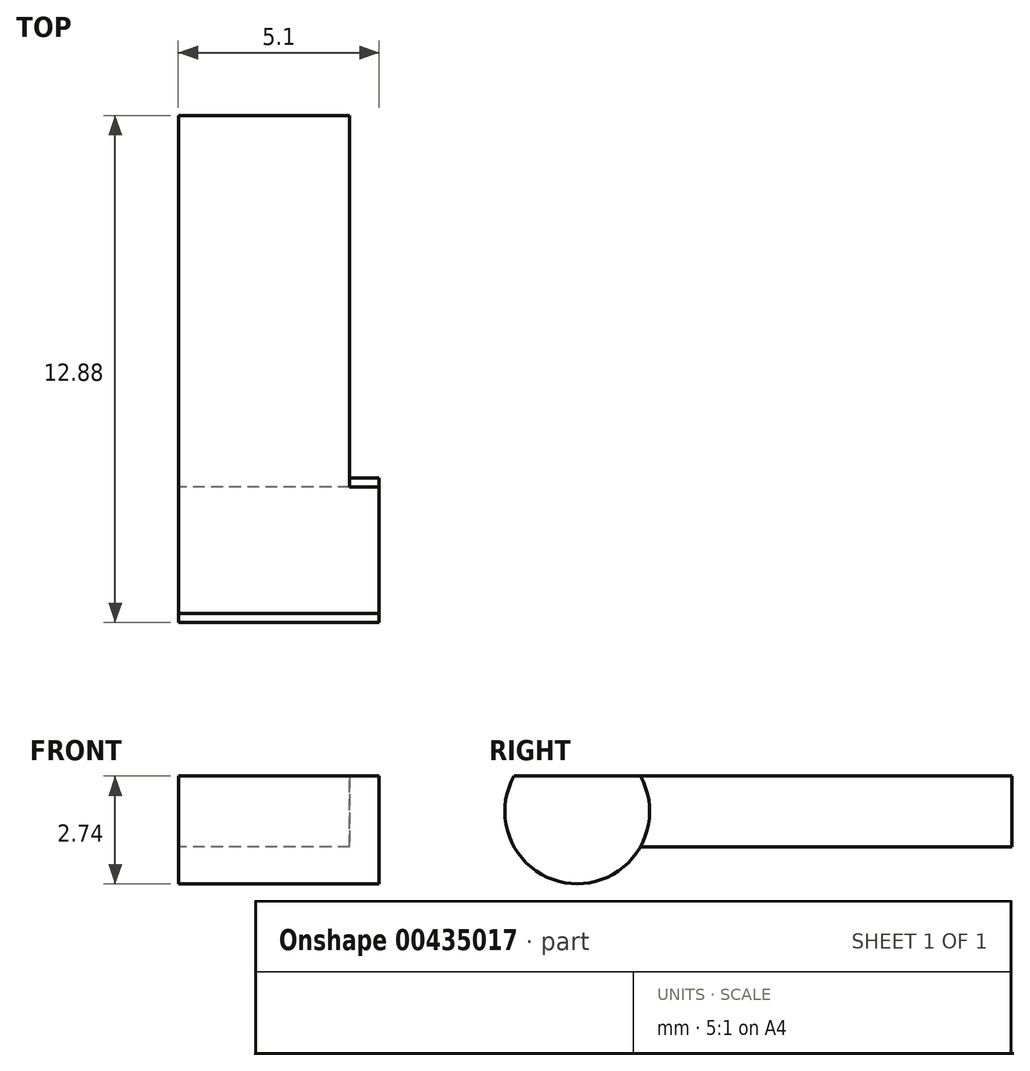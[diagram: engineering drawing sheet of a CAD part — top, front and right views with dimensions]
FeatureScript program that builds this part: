
annotation { "Feature Type Name" : "Feature", "Feature Type Description" : "" }
export const myFeature = defineFeature(function(context is Context, id is Id, definition is map)
    precondition{}
    {
        {
            var Q0;
            Q0=qCreatedBy(makeId("Front.planeOp"),FACE);
            var sketch = newSketch(context, id + "F0", { "sketchPlane" : qUnion([Q0])});
            skLineSegment(sketch, "E0.bottom", {"start": v(-14.26, 26.76) * mm, "end": v(-9.9, 26.76) * mm});
            skLineSegment(sketch, "E0.top", {"start": v(-14.26, 24.96) * mm, "end": v(-9.9, 24.96) * mm});
            skLineSegment(sketch, "E0.left", {"start": v(-14.26, 26.76) * mm, "end": v(-14.26, 24.96) * mm});
            skLineSegment(sketch, "E0.right", {"start": v(-9.9, 26.76) * mm, "end": v(-9.9, 24.96) * mm});
            skSolve(sketch);
        }
        {
            var Q0;
            Q0 = qSketchRegion(id + "F0", true);
            extrude(context, id + "F1", {"entities" : qUnion([Q0]), "depth" : 11.7 * mm, "offsetDistance" : 25 * mm});
        }
        {
            var Q0;
            Q0=makeQuery(id+"F1.opExtrude","SWEPT_FACE",FACE,{"disambiguationData":[OSD([sQuery(id+"F0.wireOp",EDGE,"E0.left")])]});
            var sketch = newSketch(context, id + "F2", { "sketchPlane" : qUnion([Q0])});
            skCircle(sketch, "E1", {"center": v(11.04, 25.86) * mm, "radius": 1.84 * mm});
            skPoint(sketch, "E1.centerSnap0", {"position": v(11.7, 25.86) * mm});
            skSolve(sketch);
        }
        {
            var Q0;
            Q0 = qSketchRegion(id + "F2", true);
            extrude(context, id + "F3", {"entities" : qUnion([Q0]), "operationType" : NewBodyOperationType.ADD, "oppositeDirection" : true, "depth" : 5.1 * mm, "offsetDistance" : 25 * mm});
        }
        {
            var Q0;
            Q0=makeQuery(id+"F3.boolean.opBoolean","MERGE",FACE,{"derivedFrom":[makeQuery(id+"F1.opExtrude","SWEPT_FACE",FACE,{"disambiguationData":[OSD([sQuery(id+"F0.wireOp",EDGE,"E0.left")])]}),makeQuery(id+"F3.opExtrude","CAP_FACE",FACE,{"disambiguationData":[OSD([sQuery(id+"F2.wireOp",EDGE,"E1")])],"isStart":true})]});
            var sketch = newSketch(context, id + "F4", { "sketchPlane" : qUnion([Q0])});
            skLineSegment(sketch, "E2", {"start": v(9.44, 26.76) * mm, "end": v(31.72, 26.76) * mm});
            skLineSegment(sketch, "E3", {"start": v(31.72, 26.76) * mm, "end": v(10.56, 28.52) * mm});
            skLineSegment(sketch, "E4", {"start": v(10.56, 28.52) * mm, "end": v(9.44, 26.76) * mm});
            skSolve(sketch);
        }
        {
            var Q0;
            Q0 = qSketchRegion(id + "F4", true);
            extrude(context, id + "F5", {"entities" : qUnion([Q0]), "operationType" : NewBodyOperationType.REMOVE, "oppositeDirection" : true, "depth" : 25 * mm, "offsetDistance" : 25 * mm});
        }
        {
            var Q0;
            Q0=makeQuery(id+"F5.boolean.opBoolean","COPY",FACE,{"derivedFrom":makeQuery(id+"F5.opExtrude","SWEPT_FACE",FACE,{"disambiguationData":[OSD([sQuery(id+"F4.wireOp",EDGE,"E4")])]})});
            var sketch = newSketch(context, id + "F6", { "sketchPlane" : qUnion([Q0])});
            skLineSegment(sketch, "E5", {"start": v(-14.26, 27.66) * mm, "end": v(-9.16, 27.66) * mm});
            skLineSegment(sketch, "E6", {"start": v(-9.16, 27.66) * mm, "end": v(-9.16, 27.86) * mm});
            skLineSegment(sketch, "E7", {"start": v(-9.16, 27.86) * mm, "end": v(-14.26, 27.86) * mm});
            skLineSegment(sketch, "E8", {"start": v(-14.26, 27.86) * mm, "end": v(-14.26, 27.66) * mm});
            skSolve(sketch);
        }
        {
            var Q0;
            Q0 = qSketchRegion(id + "F6", true);
            extrude(context, id + "F7", {"entities" : qUnion([Q0]), "operationType" : NewBodyOperationType.REMOVE, "oppositeDirection" : true, "depth" : 25 * mm, "offsetDistance" : 25 * mm});
        }
    });
